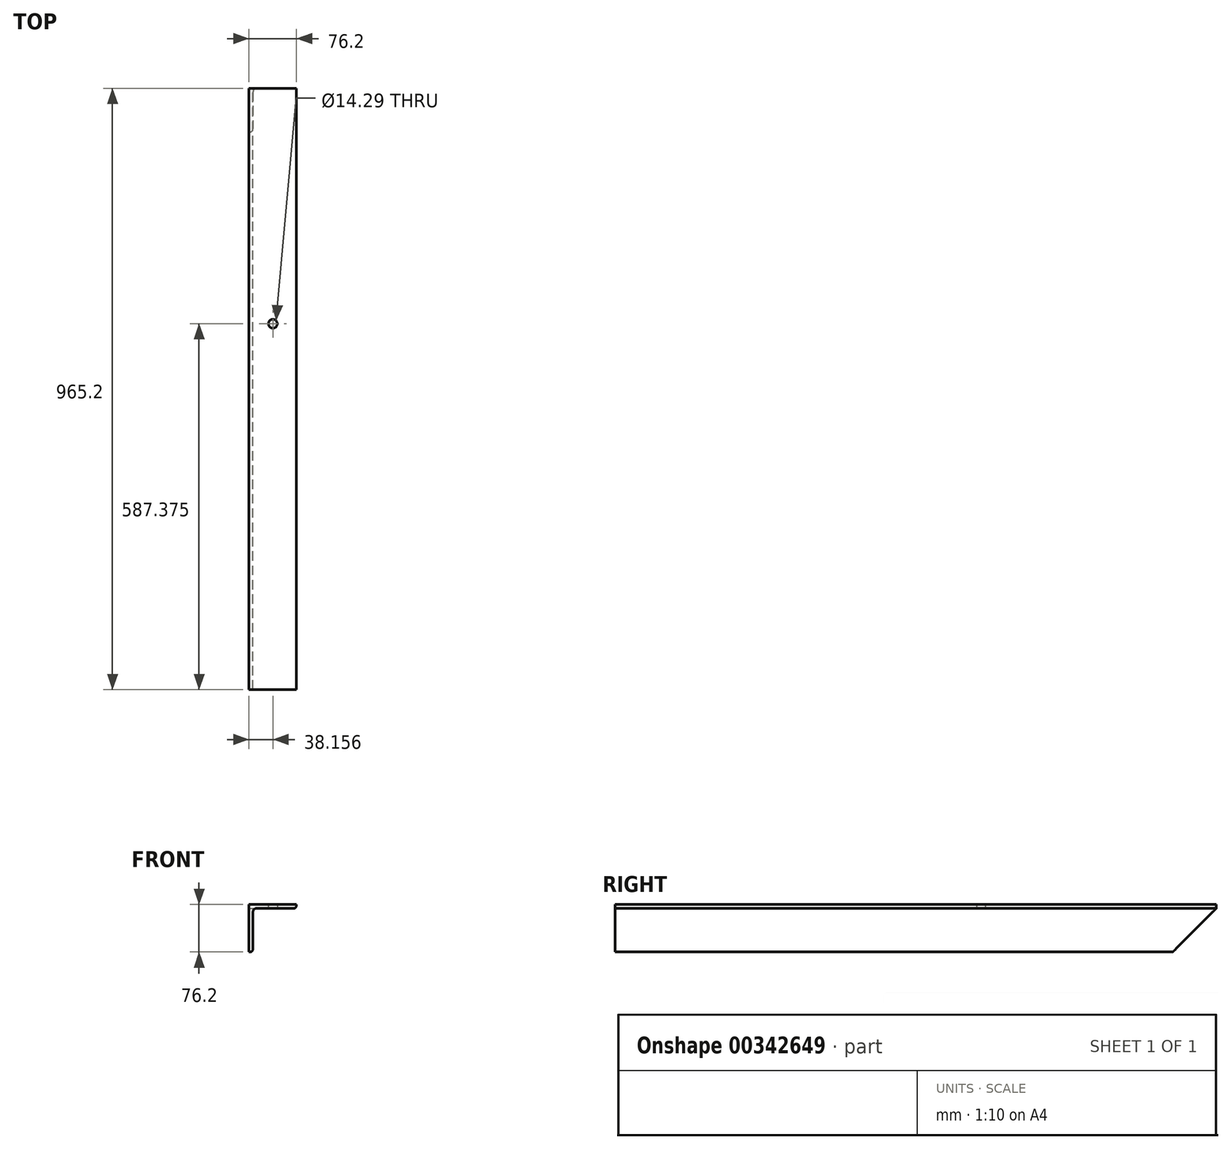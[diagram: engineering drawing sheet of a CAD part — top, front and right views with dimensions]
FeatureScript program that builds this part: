
annotation { "Feature Type Name" : "Feature", "Feature Type Description" : "" }
export const myFeature = defineFeature(function(context is Context, id is Id, definition is map)
    precondition{}
    {
        {
            var Q0;
            Q0=qCreatedBy(makeId("Front.planeOp"),FACE);
            var sketch = newSketch(context, id + "F0", { "sketchPlane" : qUnion([Q0])});
            skLineSegment(sketch, "E0", {"start": v(0, 0) * mm, "end": v(-6.35, 0) * mm});
            skLineSegment(sketch, "E1", {"start": v(-6.35, 0) * mm, "end": v(-6.35, 76.2) * mm});
            skLineSegment(sketch, "E2", {"start": v(-6.35, 76.2) * mm, "end": v(69.85, 76.2) * mm});
            skLineSegment(sketch, "E3", {"start": v(69.85, 76.2) * mm, "end": v(69.85, 69.85) * mm});
            skLineSegment(sketch, "E4", {"start": v(69.85, 69.85) * mm, "end": v(0, 69.85) * mm});
            skLineSegment(sketch, "E5", {"start": v(0, 69.85) * mm, "end": v(0, 0) * mm});
            skSolve(sketch);
        }
        {
            var Q0;
            Q0 = qSketchRegion(id + "F0", true);
            extrude(context, id + "F1", {"entities" : qUnion([Q0]), "endBound" : BoundingType.SYMMETRIC, "depth" : 965.2 * mm});
        }
        {
            var Q0;
            Q0=qCreatedBy(makeId("Right.planeOp"),FACE);
            var sketch = newSketch(context, id + "F2", { "sketchPlane" : qUnion([Q0])});
            skPoint(sketch, "E6.0", {"position": v(482.6, 69.85) * mm});
            skLineSegment(sketch, "E7", {"start": v(482.6, 69.85) * mm, "end": v(412.75, 0) * mm});
            skLineSegment(sketch, "E8", {"start": v(412.75, 0) * mm, "end": v(482.6, 0) * mm});
            skLineSegment(sketch, "E9", {"start": v(482.6, 0) * mm, "end": v(482.6, 69.85) * mm});
            skSolve(sketch);
        }
        {
            var Q0;
            Q0 = qSketchRegion(id + "F2", true);
            extrude(context, id + "F3", {"entities" : qUnion([Q0]), "operationType" : NewBodyOperationType.REMOVE, "endBound" : BoundingType.THROUGH_ALL, "oppositeDirection" : true, "depth" : 25.4 * mm});
        }
        {
            var Q0;
            Q0=qCreatedBy(makeId("Top.planeOp"),FACE);
            var sketch = newSketch(context, id + "F4", { "sketchPlane" : qUnion([Q0])});
            skPoint(sketch, "E10.0", {"position": v(-6.35, 482.6) * mm});
            skCircle(sketch, "E11", {"center": v(31.8, 104.78) * mm, "radius": 7.14 * mm});
            skSolve(sketch);
        }
        {
            var Q0;
            Q0=makeQuery(id+"F1.opExtrude","SWEPT_EDGE",EDGE,{"disambiguationData":[OSD([sQuery(id+"F0.wireOp",EDGE,"E4"),sQuery(id+"F0.wireOp",EDGE,"E5")])]});
            var Q1;
            Q1=makeQuery(id+"F1.opExtrude","SWEPT_EDGE",EDGE,{"disambiguationData":[OSD([sQuery(id+"F0.wireOp",EDGE,"E3"),sQuery(id+"F0.wireOp",EDGE,"E4")])]});
            var Q2;
            Q2=makeQuery(id+"F1.opExtrude","SWEPT_EDGE",EDGE,{"disambiguationData":[OSD([sQuery(id+"F0.wireOp",EDGE,"E0"),sQuery(id+"F0.wireOp",EDGE,"E5")])]});
            fillet(context, id + "F5", {"entities" : qUnion([Q0, Q1, Q2]), "radius" : 5.08 * mm, "tangentPropagation" : true, "allowEdgeOverflow" : false});
        }
        {
            var Q0;
            Q0 = qSketchRegion(id + "F4", true);
            extrude(context, id + "F6", {"entities" : qUnion([Q0]), "operationType" : NewBodyOperationType.REMOVE, "depth" : 101.6 * mm, "offsetDistance" : 25.4 * mm});
        }
    });
